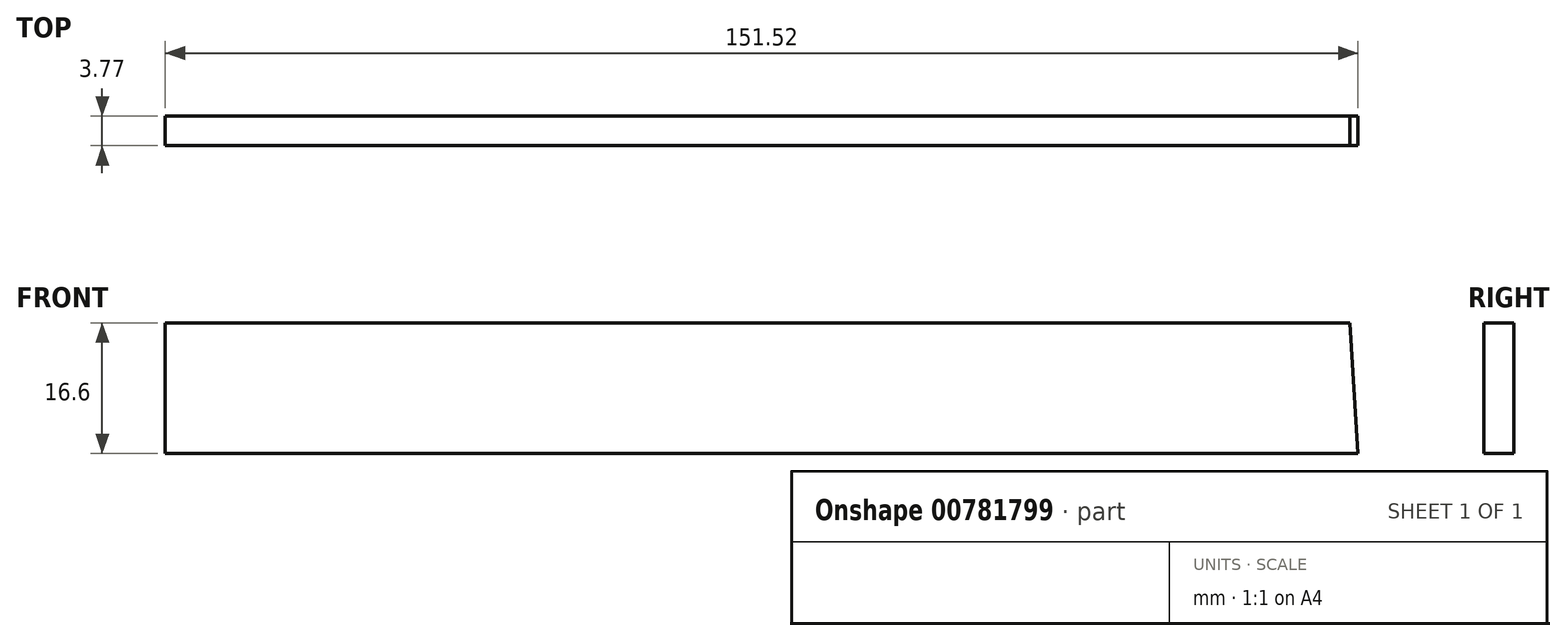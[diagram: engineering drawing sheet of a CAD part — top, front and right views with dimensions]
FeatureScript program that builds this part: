
annotation { "Feature Type Name" : "Feature", "Feature Type Description" : "" }
export const myFeature = defineFeature(function(context is Context, id is Id, definition is map)
    precondition{}
    {
        {
            var Q0;
            Q0=qCreatedBy(makeId("Front.planeOp"),FACE);
            var sketch = newSketch(context, id + "F0", { "sketchPlane" : qUnion([Q0])});
            skLineSegment(sketch, "E0", {"start": v(78.35, -16.6) * mm, "end": v(-73.17, -16.6) * mm});
            skLineSegment(sketch, "E1", {"start": v(-73.17, -16.6) * mm, "end": v(-73.17, 0) * mm});
            skLineSegment(sketch, "E2", {"start": v(-73.17, 0) * mm, "end": v(77.28, 0) * mm});
            skLineSegment(sketch, "E3", {"start": v(77.28, 0) * mm, "end": v(78.35, -16.6) * mm});
            skSolve(sketch);
        }
        {
            var Q0;
            Q0=makeQuery(id+"F0.imprint","IMPRINT",FACE,{"disambiguationData":[TD([[makeQuery(id+"F0.imprint","IMPRINT",EDGE,{"derivedFrom":sQuery(id+"F0.wireOp",EDGE,"E0")}),-1.0]])]});
            extrude(context, id + "F1", {"entities" : qUnion([Q0]), "depth" : 3.77 * mm, "offsetDistance" : 25.4 * mm});
        }
    });
